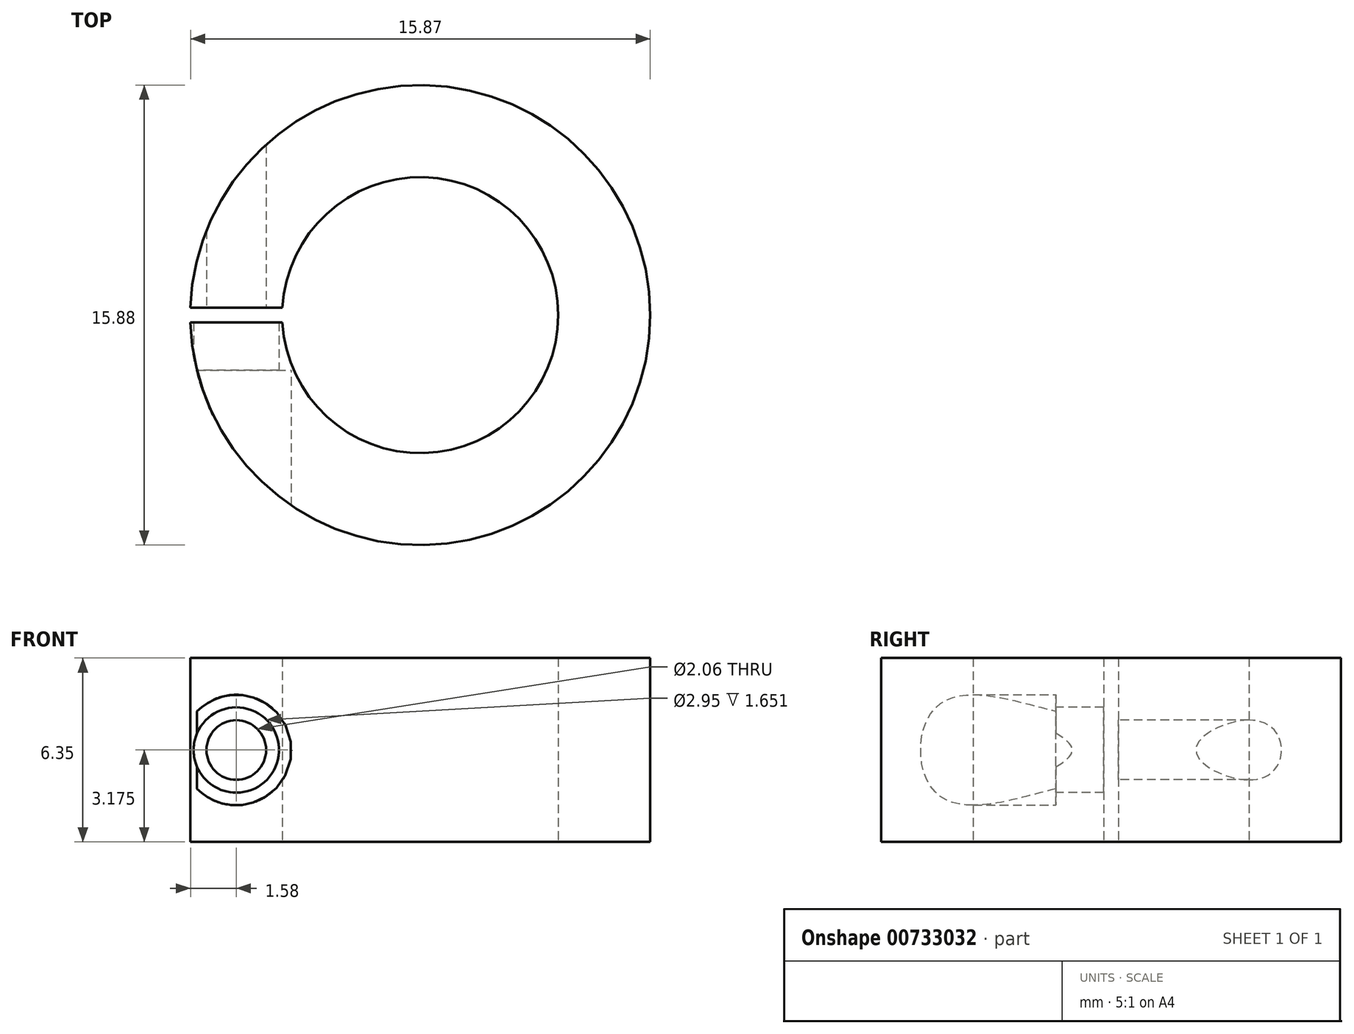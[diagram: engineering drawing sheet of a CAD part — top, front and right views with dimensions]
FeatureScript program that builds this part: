
annotation { "Feature Type Name" : "Feature", "Feature Type Description" : "" }
export const myFeature = defineFeature(function(context is Context, id is Id, definition is map)
    precondition{}
    {
        {
            var Q0;
            Q0=qCreatedBy(makeId("Top.planeOp"),FACE);
            var sketch = newSketch(context, id + "F0", { "sketchPlane" : qUnion([Q0])});
            skCircle(sketch, "E0", {"center": v(0, 0) * mm, "radius": 7.94 * mm});
            skCircle(sketch, "E1", {"center": v(0, 0) * mm, "radius": 4.76 * mm});
            skSolve(sketch);
        }
        {
            var Q0;
            Q0=makeQuery(id+"F0.imprint","IMPRINT",FACE,{"disambiguationData":[TD([[makeQuery(id+"F0.imprint","IMPRINT",EDGE,{"derivedFrom":sQuery(id+"F0.wireOp",EDGE,"E0")}),1.0]])]});
            extrude(context, id + "F1", {"entities" : qUnion([Q0]), "depth" : 6.35 * mm, "offsetDistance" : 25.4 * mm});
        }
        {
            var Q0;
            Q0=qCreatedBy(makeId("Front.planeOp"),FACE);
            cPlane(context, id + "F2", {"entities" : qUnion([Q0]), "cplaneType" : CPlaneType.OFFSET, "offset" : 1.9 * mm, "width" : 152.4 * mm, "height" : 152.4 * mm});
        }
        {
            var Q0;
            Q0=qCreatedBy(id+"F2.planeOp",FACE);
            var sketch = newSketch(context, id + "F3", { "sketchPlane" : qUnion([Q0])});
            skCircle(sketch, "E2", {"center": v(-6.35, 3.18) * mm, "radius": 1.9 * mm});
            skSolve(sketch);
        }
        {
            var Q0;
            Q0 = qSketchRegion(id + "F3", true);
            extrude(context, id + "F4", {"entities" : qUnion([Q0]), "operationType" : NewBodyOperationType.REMOVE, "depth" : 25.4 * mm, "offsetDistance" : 25.4 * mm});
        }
        {
            var Q0;
            Q0=qCreatedBy(makeId("Front.planeOp"),FACE);
            var sketch = newSketch(context, id + "F5", { "sketchPlane" : qUnion([Q0])});
            skLineSegment(sketch, "E3.bottom", {"start": v(-7.95, 0) * mm, "end": v(-4.73, 0) * mm});
            skLineSegment(sketch, "E3.top", {"start": v(-7.95, 6.37) * mm, "end": v(-4.73, 6.37) * mm});
            skLineSegment(sketch, "E3.left", {"start": v(-7.95, 0) * mm, "end": v(-7.95, 6.37) * mm});
            skLineSegment(sketch, "E3.right", {"start": v(-4.73, 0) * mm, "end": v(-4.73, 6.37) * mm});
            skSolve(sketch);
        }
        {
            var Q0;
            Q0 = qSketchRegion(id + "F5", true);
            extrude(context, id + "F6", {"entities" : qUnion([Q0]), "operationType" : NewBodyOperationType.REMOVE, "endBound" : BoundingType.SYMMETRIC, "oppositeDirection" : true, "depth" : 0.5 * mm, "offsetDistance" : 25.4 * mm});
        }
        {
            var Q0;
            Q0=makeQuery(id+"F4.boolean.opBoolean","COPY",FACE,{"derivedFrom":makeQuery(id+"F4.opExtrude","CAP_FACE",FACE,{"disambiguationData":[OSD([sQuery(id+"F3.wireOp",EDGE,"E2")])],"isStart":true})});
            var sketch = newSketch(context, id + "F7", { "sketchPlane" : qUnion([Q0])});
            skCircle(sketch, "E4", {"center": v(-6.35, 3.18) * mm, "radius": 1.47 * mm});
            skCircle(sketch, "E5", {"center": v(-6.35, 3.18) * mm, "radius": 1.03 * mm});
            skSolve(sketch);
        }
        {
            var Q0;
            Q0=makeQuery(id+"F7.imprint","IMPRINT",FACE,{"disambiguationData":[TD([[makeQuery(id+"F7.imprint","IMPRINT",EDGE,{"derivedFrom":sQuery(id+"F7.wireOp",EDGE,"E5")}),1.0]])]});
            extrude(context, id + "F8", {"entities" : qUnion([Q0]), "operationType" : NewBodyOperationType.REMOVE, "oppositeDirection" : true, "depth" : 25.4 * mm, "offsetDistance" : 25.4 * mm});
        }
        {
            var Q0;
            Q0 = qSketchRegion(id + "F7", true);
            extrude(context, id + "F9", {"entities" : qUnion([Q0]), "operationType" : NewBodyOperationType.REMOVE, "oppositeDirection" : true, "depth" : 1.78 * mm, "offsetDistance" : 25.4 * mm});
        }
    });
